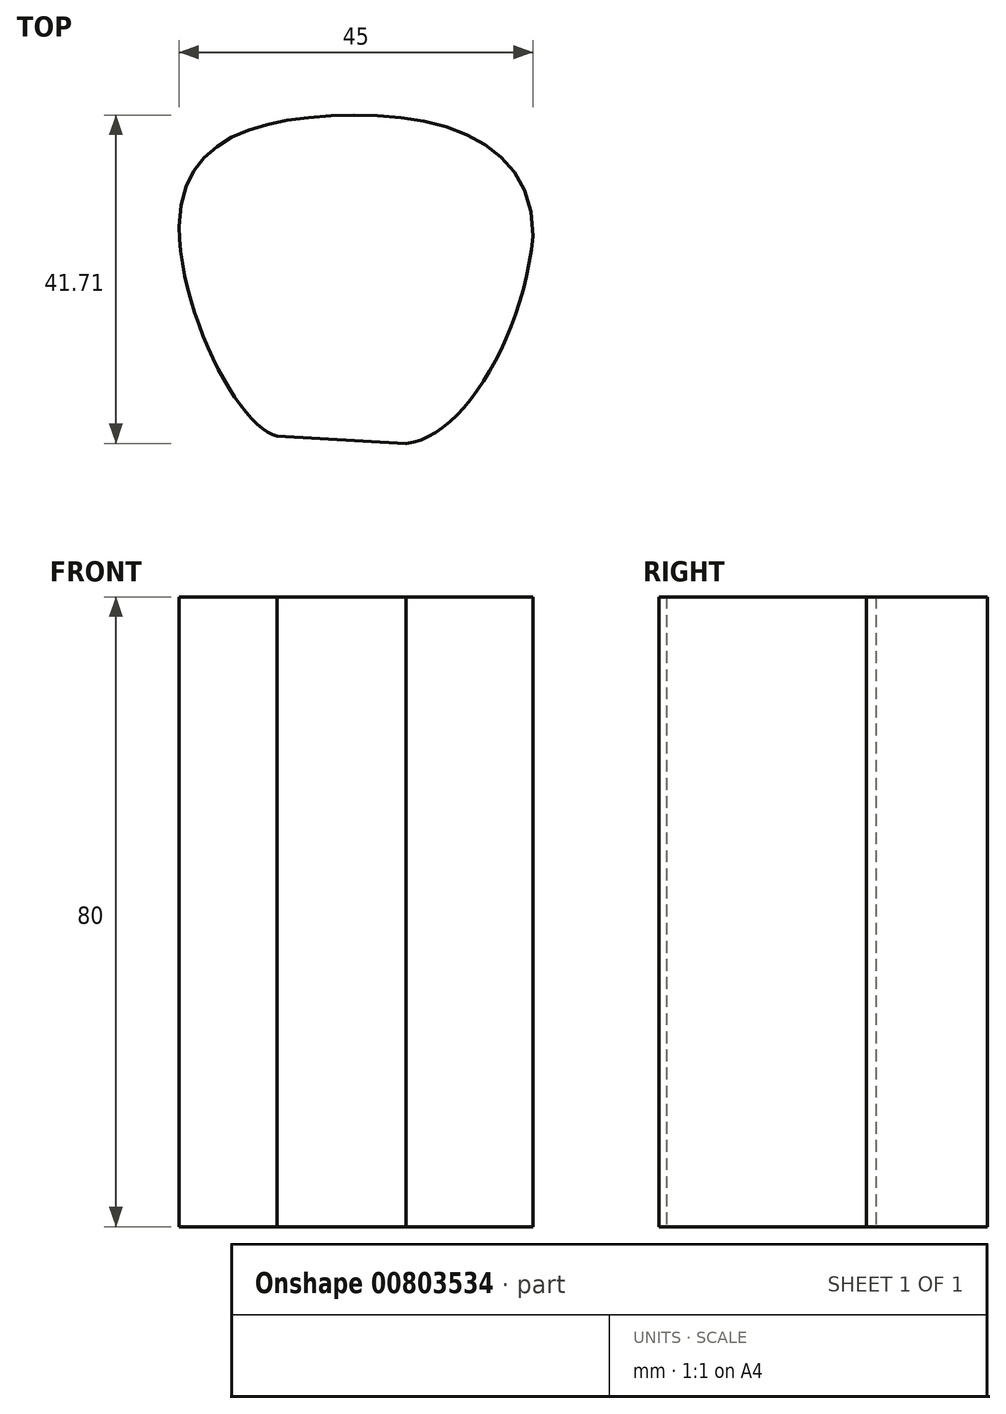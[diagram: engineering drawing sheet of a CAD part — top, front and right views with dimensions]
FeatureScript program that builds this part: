
annotation { "Feature Type Name" : "Feature", "Feature Type Description" : "" }
export const myFeature = defineFeature(function(context is Context, id is Id, definition is map)
    precondition{}
    {
        {
            var Q0;
            Q0=qCreatedBy(makeId("Top.planeOp"),FACE);
            var sketch = newSketch(context, id + "F0", { "sketchPlane" : qUnion([Q0])});
            skLineSegment(sketch, "E0", {"start": v(-20.67, -1.31) * mm, "end": v(-37.07, -0.35) * mm});
            skFitSpline(sketch, "E1", {"points": [v(-20.67, -1.31) * mm, v(-4.56, 25.01) * mm], "startDerivative": vector(21.2, 2.34) * mm, "endDerivative": vector(4.01, 39.45) * mm});
            skFitSpline(sketch, "E2", {"points": [v(-4.56, 25.01) * mm, v(-31.08, 40.26) * mm, v(-49.56, 26.23) * mm], "startDerivative": vector(-0.1, 77.18) * mm, "endDerivative": vector(-1.27, -66.51) * mm});
            skFitSpline(sketch, "E3", {"points": [v(-49.56, 26.23) * mm, v(-37.07, -0.35) * mm], "startDerivative": vector(0.66, -34.97) * mm, "endDerivative": vector(13.17, -2.04) * mm});
            skLineSegment(sketch, "E4", {"start": v(-28.87, -0.83) * mm, "end": v(-28.87, 40.37) * mm, "construction": true});
            skLineSegment(sketch, "E5", {"start": v(-28.87, 19.77) * mm, "end": v(-48.76, 19.77) * mm, "construction": true});
            skLineSegment(sketch, "E6", {"start": v(-28.87, 19.77) * mm, "end": v(-5.43, 19.77) * mm, "construction": true});
            skSolve(sketch);
        }
        {
            var Q0;
            Q0=qSketchRegion(id+"F0",true);
            extrude(context, id + "F1", {"entities" : qUnion([Q0]), "endBound" : BoundingType.SYMMETRIC, "depth" : 80 * mm, "offsetDistance" : 25 * mm});
        }
    });
